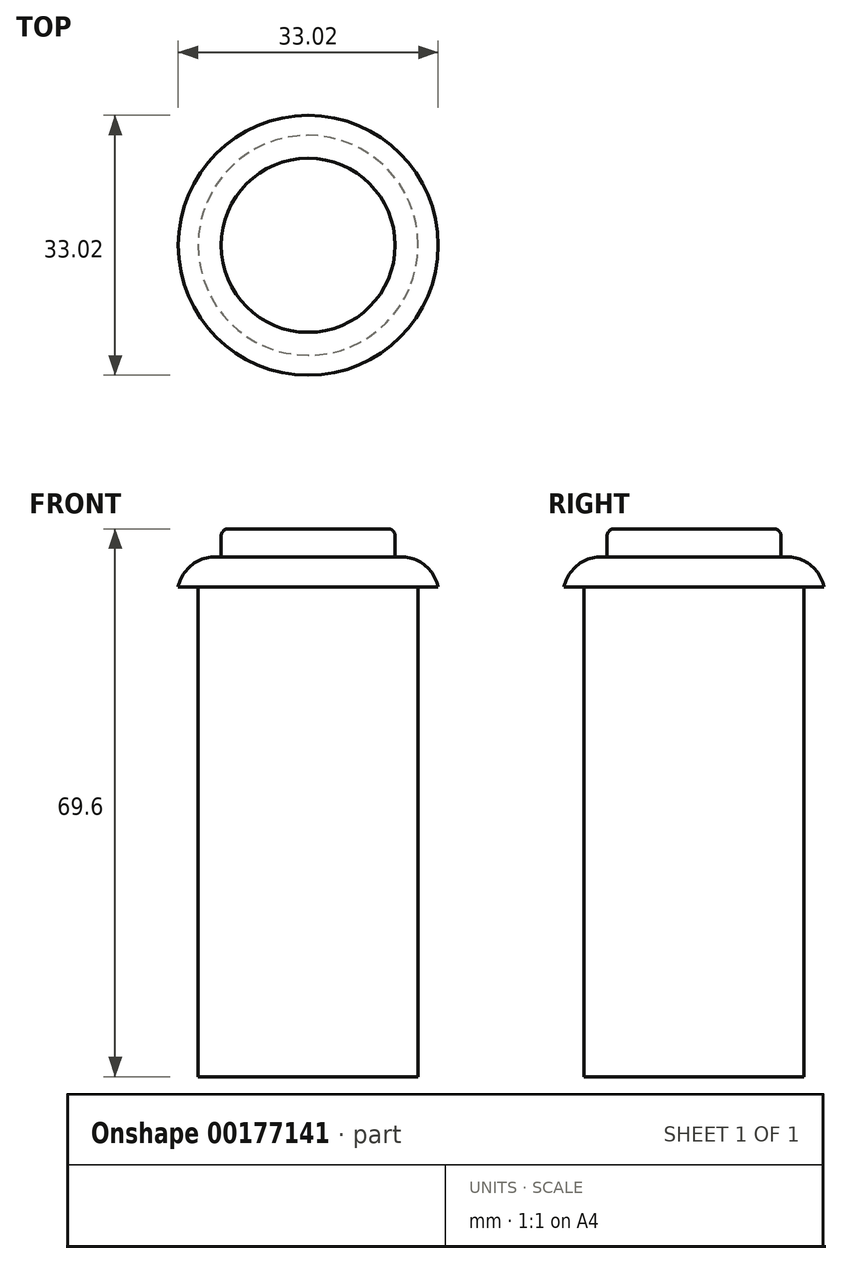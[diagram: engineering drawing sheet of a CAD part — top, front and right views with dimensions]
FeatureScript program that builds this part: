
annotation { "Feature Type Name" : "Feature", "Feature Type Description" : "" }
export const myFeature = defineFeature(function(context is Context, id is Id, definition is map)
    precondition{}
    {
        {
            var Q0;
            Q0=qCreatedBy(makeId("Top.planeOp"),FACE);
            var sketch = newSketch(context, id + "F0", { "sketchPlane" : qUnion([Q0])});
            skCircle(sketch, "E0", {"center": v(0, 0) * mm, "radius": 16.51 * mm});
            skCircle(sketch, "E1", {"center": v(0, 0) * mm, "radius": 11.05 * mm});
            skSolve(sketch);
        }
        {
            var Q0;
            Q0 = qSketchRegion(id + "F0", true);
            extrude(context, id + "F1", {"entities" : qUnion([Q0]), "depth" : 3.8 * mm});
        }
        {
            var Q0;
            Q0=makeQuery(id+"F0.imprint","IMPRINT",FACE,{"disambiguationData":[TD([[makeQuery(id+"F0.imprint","IMPRINT",EDGE,{"derivedFrom":sQuery(id+"F0.wireOp",EDGE,"E1")}),1.0]])]});
            extrude(context, id + "F2", {"entities" : qUnion([Q0]), "operationType" : NewBodyOperationType.ADD, "depth" : 7.37 * mm});
        }
        {
            var Q0;
            Q0=makeQuery(id+"F1.opExtrude","CAP_EDGE",EDGE,{"disambiguationData":[OSD([sQuery(id+"F0.wireOp",EDGE,"E0")])],"isStart":false});
            fillet(context, id + "F3", {"entities" : qUnion([Q0]), "radius" : 4.83 * mm, "tangentPropagation" : true, "allowEdgeOverflow" : false});
        }
        {
            var Q0;
            Q0=makeQuery(id+"F2.opExtrude","CAP_EDGE",EDGE,{"disambiguationData":[OSD([sQuery(id+"F0.wireOp",EDGE,"E1")])],"isStart":false});
            fillet(context, id + "F4", {"entities" : qUnion([Q0]), "radius" : 0.89 * mm, "tangentPropagation" : true, "allowEdgeOverflow" : false});
        }
        {
            var Q0;
            Q0=makeQuery(id+"F0.imprint","IMPRINT",FACE,{"disambiguationData":[TD([[makeQuery(id+"F0.imprint","IMPRINT",EDGE,{"derivedFrom":sQuery(id+"F0.wireOp",EDGE,"E1")}),1.0]])]});
            var sketch = newSketch(context, id + "F5", { "sketchPlane" : qUnion([Q0])});
            skCircle(sketch, "E2", {"center": v(0, 0) * mm, "radius": 13.97 * mm});
            skSolve(sketch);
        }
        {
            var Q0;
            Q0=makeQuery(id+"F5.imprint","IMPRINT",FACE,{"disambiguationData":[TD([[makeQuery(id+"F5.imprint","IMPRINT",EDGE,{"derivedFrom":sQuery(id+"F5.wireOp",EDGE,"E2")}),1.0]])]});
            var Q1;
            Q1=makeQuery(id+"F5.imprint","IMPRINT",FACE,{"disambiguationData":[TD([[makeQuery(id+"F5.imprint","IMPRINT",EDGE,{"derivedFrom":makeQuery(id+"F0.imprint","IMPRINT",EDGE,{"derivedFrom":sQuery(id+"F0.wireOp",EDGE,"E1")})}),1.0]])]});
            extrude(context, id + "F6", {"entities" : qUnion([Q0, Q1]), "operationType" : NewBodyOperationType.ADD, "oppositeDirection" : true, "depth" : 62.23 * mm});
        }
    });
